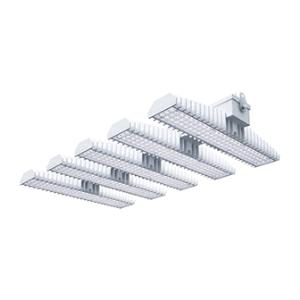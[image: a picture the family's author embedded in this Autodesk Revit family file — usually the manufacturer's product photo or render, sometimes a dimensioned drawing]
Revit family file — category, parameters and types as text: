
# Revit family: 3f_filippi_-_3f_lem_ho_ampio_3f_filippi_-_58958_a0811_-_3f_lem_5_ho_led_350_cr_ampio___vt_7f6d
name_source: partatom
category: Lighting Fixtures
units: mm (PartAtom-declared; Revit-internal decimal feet)

## family parameters
Cut with Voids When Loaded = No
Host = Face
Light Source = No
Part Type = Normal
Room Calculation Point = No
Round Connector Dimension = Use Diameter
Shared = No

## types (1)
- 3F Filippi - 3F LEM HO Ampio (1 x LED, 52628 lm, 345 W, 4000 K)
    Apparent Load = 345 VA
    Approval mark = CE
    CIE Flux Codes = 60 92 99 100 100
    Color Rendering = 80
    Color Temperature = 4000 K
    Control Gear = Electronic ballast
    Default Elevation = 1800 mm
    Description = Industrial luminaire with high light output and high luminous efficiency designed with the most innovative technologies for environments with temperature up to 55°C.

ILLUMINOTECHNICAL
Luminous efficiency 100% (DLOR 99%, ULOR 1%).
Initial luminous flux of the luminaire 52628 lm.
Direct symmetric wide distribution: the illuminated area has a rectangular shape.
Installation Interdistance Transv.D = 1.58 x hu - Long.D = 1.45 x hu.
Tabular UGR (CIE 117 - 4H-8H; S=0.25H; 70/50/20): RUG 23.9 - 24.9.
Beam angle: 93° - 99°.
Luminous efficacy 153 lm/W.
Lifetime (L93/B10): 30000 h. (tq+25°C)
Lifetime (L90/B10): 50000 h. (tq+25°C)
Lifetime (L85/B10): 80000 h. (tq+25°C)
Lifetime (L80/B10): 100000 h. (tq+25°C)
Lifetime (L85/B10): 50000 h. (tq+55°C)
Sudden decreased luminous flux after 50000 hours: 0% (C0).
Photobiological safety in compliance with IEC/TR 62778: RG0 risk exempt, (IEC 62471).
In compliance with IEC/EN 62722-2-1 - IEC/EN 62717 standards.

SOURCE
5 Mid-Power linear LED modules 70W/840.
Energy efficiency class (UE 2019/2020 - UE 2019/2015): C.
CIE 13.3 Colour rendering index: CRI >80 (R9 <50%).
IES TM-30 Fidelity Index: Rf = 84 Rg = 95.
CCT nominal colour temperature 4000 K.
Colour initial tolerance (MacAdam): SDCM 3.

MECHANICAL
Passive modular heatsinks in die-casted aluminium, painted in white colour.
To optimize the thermal management of the LED module, the heatsinks are oversized and provided with self-cleaning of cooling fins.
Wiring body in aluminium and galvanised steel anchored solidly to the sinks and thermally separated.
3F Lens lenses with high luminous efficiency, transparent methacrylate (PMMA), fixed to the LED modules.
Fixing brackets in stainless steel.
Luminaire with limited surface temperature. - D - (EN 60598-2-24)
Dimensions: 952x542 mm, height 133 mm. Weight 24.43 kg.
IP65 protection degree.
Mechanical strength to impacts IK06 (1 joule).
Glow-wire test resistance 650°C.

ELECTRICAL
Halogen Free electronic wiring 230V-50/60Hz, power factor 0.97, THD <25%, constant output current, class I, 3 driver.
Power of the luminaire 345 W.
ENEC - CE.
SAFE FLICKER: PstLM=<1 and SVM=<0.4 (IEC TR 61547-1 and IEC TR 63158), to ensure a more comfortable and safe light.
Luminaire compliant with EN 60598-2-22 for power supply from a centralised emergency system CPSS (Central Power Supply System), not incorporated in the luminaire - high risk areas excluded. The default power and flux are 100% in AC and 100% in DC.
Ambient temperature from -30°C to +55°C.
Temperature class T6 max 85°C.
Quick connection via M20 3P connector with 9-13 mm tightening range.
Power unit positioned on a separate compartment by the LED module to ensure optimum temperatures of cabling components, to be inspectable and maintainable.
Relative humidity UR: <85%.

INSTALLATION
Ceiling / Suspended / Wall.
All accessories dedicated to this product are available on the Catalog and on our website www.3F-Filippi.com.

ACCESSORIES
A0811 - VT transparent glass, tempered, not flammable, with sealing gasket.
One required for each light module. The pack contains 10 pieces.

APPLICATIONS
In commercial environments, exhibition and industrial areas, stores, open areas.
Environments in which it is necessary a total protection against falling fragments (eg environments with foodstuffs or machines with moving parts or with extreme temperature changes), use luminaires with polycarbonate lenses.

WARNING
Fixture not suitable for cold stores with an ambient temperature <0°C and/or relative humidity >85%.
Luminaire designed for disposal/recycling at end-of-life.
Replaceable (LED only) light source by a professional. Replaceable control gear by a professional.
    Height = 133 mm  [stored 0.436352 ft]
    Lamp = 1 x LED
    Lamp Light Flux = 52628 lm
    Lamp Power = 345 W
    Lamp count = 1
    Length = 952 mm
    Lifetime = 50000 h
    Luminous efficacy = 153 lm/W
    Manufacturer = 3F Filippi
    ModVariant = No
    Model = 3F Filippi - 58958+A0811 - 3F LEM 5 HO LED 350 CR AMPIO + VT
    Mounting Place = Ceiling
    Mounting Type = Pendant
    Number of Poles = 1
    OnlyDefault = Yes
    Power Factor = 1
    Product Name = 3F Filippi - 3F LEM HO Ampio
    Product group = pendant luminaire
    ProductGroupID = 9
    Protection Class = Protection class I
    Protection Degree = IP 65
    RLX_Detail_Level = 1
    RLX_Emergency_Light_Flux = 0 lm
    RLX_Emergency_Type = 0
    RLX_Emergency_Type_DB = No
    RlxData = <blob elided: 126697 chars, md5=ac98d460>
    Socket = socket
    Standby Power = 0 W
    System Light Flux = 52628 lm
    System Power = 345 W
    Type Comments = Product without accessories
    Type Image = 3f_filippi_-_lem_5__a0811.jpg
    URL = http://relux.com
    VarID = ---
    Voltage = 0 V
    Weight = 0.00 kg
    Width = 542 mm

note: [stored X ft] marks values corroborated as IEEE doubles in the binary element streams (Revit-internal decimal feet)

## geometry (parser evidence)
native form markers: Blend x4, Sweep x11
no freeform markers — native parametric forms only
